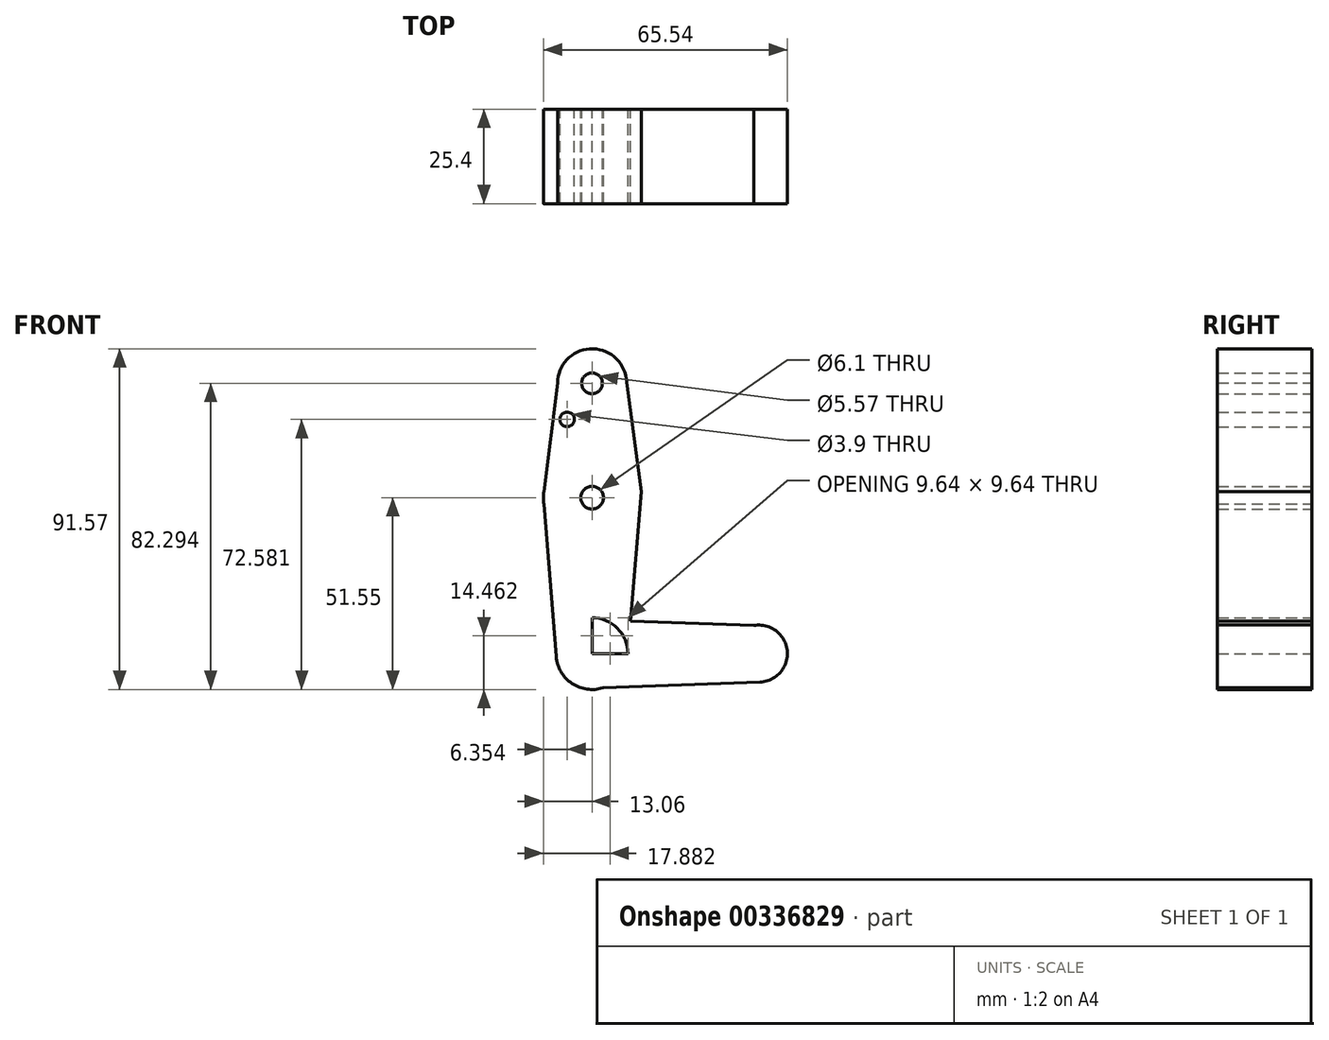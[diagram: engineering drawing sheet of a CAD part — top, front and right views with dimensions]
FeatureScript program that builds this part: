
annotation { "Feature Type Name" : "Feature", "Feature Type Description" : "" }
export const myFeature = defineFeature(function(context is Context, id is Id, definition is map)
    precondition{}
    {
        {
            var Q0;
            Q0=qCreatedBy(makeId("Front.planeOp"),FACE);
            var sketch = newSketch(context, id + "F0", { "sketchPlane" : qUnion([Q0])});
            skCircle(sketch, "E0", {"center": v(0, 0) * mm, "radius": 9.64 * mm});
            skCircle(sketch, "E1", {"center": v(0, 41.91) * mm, "radius": 13.06 * mm});
            skCircle(sketch, "E2", {"center": v(0, 72.65) * mm, "radius": 9.27 * mm});
            skCircle(sketch, "E3", {"center": v(44.8, 0) * mm, "radius": 7.68 * mm});
            skLineSegment(sketch, "E4", {"start": v(0, 72.65) * mm, "end": v(0, 0) * mm});
            skLineSegment(sketch, "E5", {"start": v(0, 0) * mm, "end": v(44.8, 0) * mm});
            skLineSegment(sketch, "E6", {"start": v(-9.27, 72.7) * mm, "end": v(-12.95, 43.55) * mm});
            skLineSegment(sketch, "E7", {"start": v(-12.95, 40.27) * mm, "end": v(-9.61, -0.78) * mm});
            skLineSegment(sketch, "E8", {"start": v(9.64, 0) * mm, "end": v(13.23, 43.55) * mm});
            skLineSegment(sketch, "E9", {"start": v(13.23, 43.55) * mm, "end": v(9.2, 73.88) * mm});
            skLineSegment(sketch, "E10", {"start": v(3.63, 8.93) * mm, "end": v(43.44, 7.55) * mm});
            skLineSegment(sketch, "E11", {"start": v(2.92, -9.2) * mm, "end": v(45.08, -7.67) * mm});
            skCircle(sketch, "E12", {"center": v(-6.7, 62.94) * mm, "radius": 1.95 * mm});
            skCircle(sketch, "E13", {"center": v(0, 72.65) * mm, "radius": 2.78 * mm});
            skCircle(sketch, "E14", {"center": v(0, 41.91) * mm, "radius": 3.05 * mm});
            skSolve(sketch);
        }
        {
            var Q0;
            Q0 = qSketchRegion(id + "F0", true);
            extrude(context, id + "F1", {"entities" : qUnion([Q0]), "depth" : 25.4 * mm});
        }
    });
